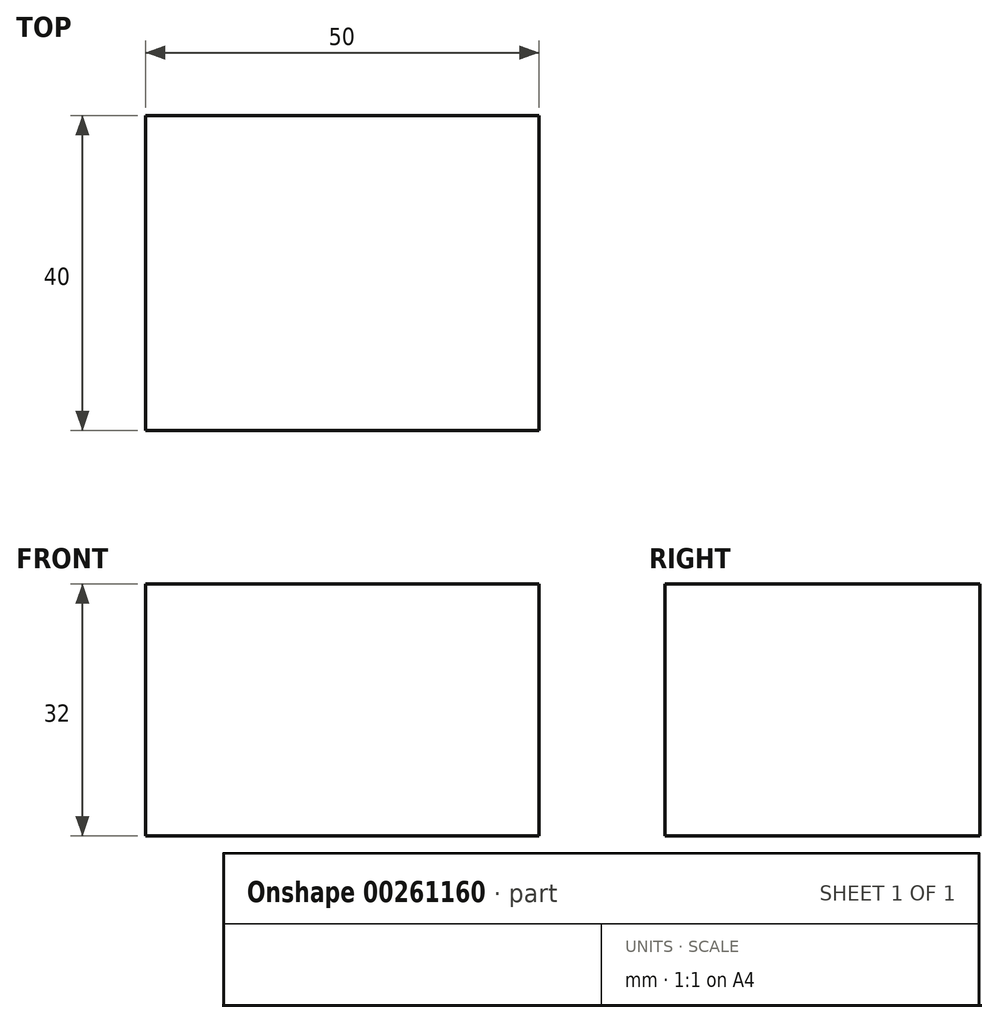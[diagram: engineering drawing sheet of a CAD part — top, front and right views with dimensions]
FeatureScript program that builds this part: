
annotation { "Feature Type Name" : "Feature", "Feature Type Description" : "" }
export const myFeature = defineFeature(function(context is Context, id is Id, definition is map)
    precondition{}
    {
        {
            var Q0;
            Q0=qCreatedBy(makeId("Front.planeOp"),FACE);
            var sketch = newSketch(context, id + "F0", { "sketchPlane" : qUnion([Q0])});
            skLineSegment(sketch, "E0.bottom", {"start": v(0, 0) * mm, "end": v(50, 0) * mm});
            skLineSegment(sketch, "E0.top", {"start": v(0, -32) * mm, "end": v(50, -32) * mm});
            skLineSegment(sketch, "E0.left", {"start": v(0, 0) * mm, "end": v(0, -32) * mm});
            skLineSegment(sketch, "E0.right", {"start": v(50, 0) * mm, "end": v(50, -32) * mm});
            skSolve(sketch);
        }
        {
            var Q0;
            Q0=makeQuery(id+"F0.imprint","IMPRINT",FACE,{"disambiguationData":[TD([[makeQuery(id+"F0.imprint","IMPRINT",EDGE,{"derivedFrom":sQuery(id+"F0.wireOp",EDGE,"E0.bottom")}),-1.0]])]});
            extrude(context, id + "F1", {"entities" : qUnion([Q0]), "depth" : 40 * mm});
        }
    });
